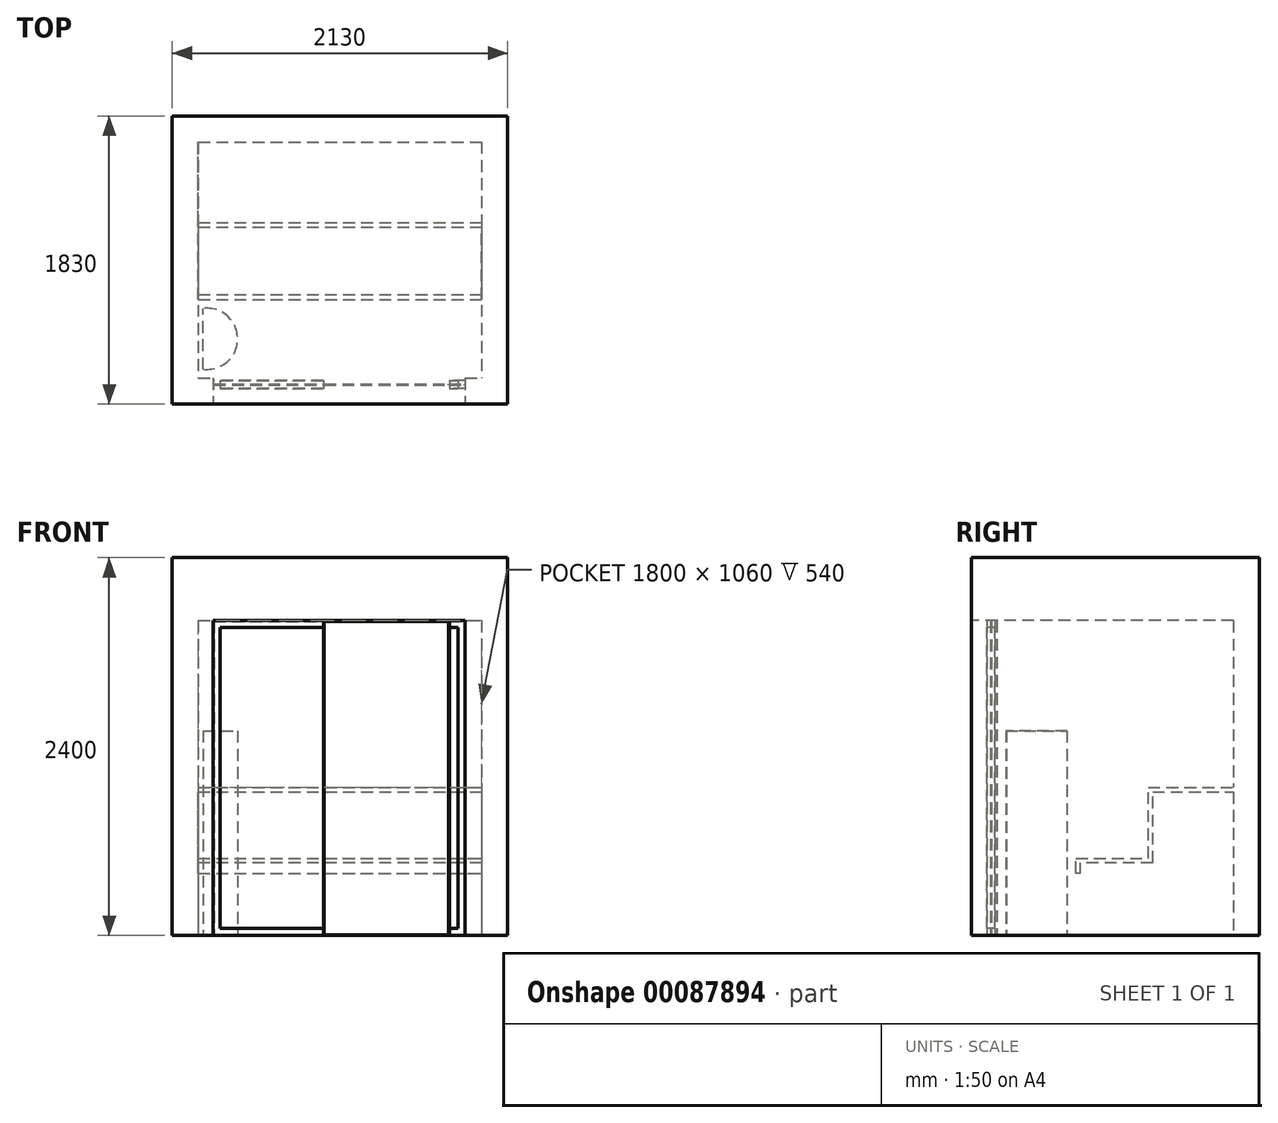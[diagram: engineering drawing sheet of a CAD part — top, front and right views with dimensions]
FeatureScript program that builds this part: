
annotation { "Feature Type Name" : "Feature", "Feature Type Description" : "" }
export const myFeature = defineFeature(function(context is Context, id is Id, definition is map)
    precondition{}
    {
        {
            var Q0;
            Q0=qCreatedBy(makeId("Top.planeOp"),FACE);
            var sketch = newSketch(context, id + "F0", { "sketchPlane" : qUnion([Q0])});
            skLineSegment(sketch, "E0.bottom", {"start": v(0, 0) * mm, "end": v(1800, 0) * mm});
            skLineSegment(sketch, "E0.top", {"start": v(0, -1500) * mm, "end": v(1800, -1500) * mm});
            skLineSegment(sketch, "E0.left", {"start": v(0, 0) * mm, "end": v(0, -1500) * mm});
            skLineSegment(sketch, "E0.right", {"start": v(1800, 0) * mm, "end": v(1800, -1500) * mm});
            skLineSegment(sketch, "E1.0", {"start": v(-165, -1665) * mm, "end": v(1965, -1665) * mm});
            skLineSegment(sketch, "E1.1", {"start": v(-165, 165) * mm, "end": v(-165, -1665) * mm});
            skLineSegment(sketch, "E1.2", {"start": v(-165, 165) * mm, "end": v(1965, 165) * mm});
            skLineSegment(sketch, "E1.3", {"start": v(1965, 165) * mm, "end": v(1965, -1665) * mm});
            skSolve(sketch);
        }
        {
            var Q0;
            Q0=makeQuery(id+"F0.imprint","IMPRINT",FACE,{"disambiguationData":[TD([[makeQuery(id+"F0.imprint","IMPRINT",EDGE,{"derivedFrom":sQuery(id+"F0.wireOp",EDGE,"E0.bottom")}),1.0]])]});
            extrude(context, id + "F1", {"entities" : qUnion([Q0]), "depth" : 2400 * mm});
        }
        {
            var Q0;
            Q0=makeQuery(id+"F1.opExtrude","SWEPT_FACE",FACE,{"disambiguationData":[OSD([sQuery(id+"F0.wireOp",EDGE,"E1.0")])]});
            var sketch = newSketch(context, id + "F2", { "sketchPlane" : qUnion([Q0])});
            skLineSegment(sketch, "E2", {"start": v(1695, 0) * mm, "end": v(1695, 2000) * mm});
            skLineSegment(sketch, "E3", {"start": v(1695, 2000) * mm, "end": v(95, 2000) * mm});
            skLineSegment(sketch, "E4", {"start": v(95, 2000) * mm, "end": v(95, 0) * mm});
            skLineSegment(sketch, "E5", {"start": v(95, 0) * mm, "end": v(1695, 0) * mm});
            skSolve(sketch);
        }
        {
            var Q0;
            Q0=makeQuery(id+"F2.imprint","IMPRINT",FACE,{"disambiguationData":[TD([[makeQuery(id+"F2.imprint","IMPRINT",EDGE,{"derivedFrom":sQuery(id+"F2.wireOp",EDGE,"E2")}),1.0]])]});
            extrude(context, id + "F3", {"entities" : qUnion([Q0]), "operationType" : NewBodyOperationType.REMOVE, "endBound" : BoundingType.UP_TO_NEXT, "oppositeDirection" : true, "depth" : 25 * mm});
        }
        {
            var Q0;
            Q0=makeQuery(id+"F1.opExtrude","CAP_FACE",FACE,{"disambiguationData":[OSD([sQuery(id+"F0.wireOp",EDGE,"E0.bottom"),sQuery(id+"F0.wireOp",EDGE,"E0.top"),sQuery(id+"F0.wireOp",EDGE,"E0.left"),sQuery(id+"F0.wireOp",EDGE,"E0.right"),sQuery(id+"F0.wireOp",EDGE,"E1.0"),sQuery(id+"F0.wireOp",EDGE,"E1.1"),sQuery(id+"F0.wireOp",EDGE,"E1.2"),sQuery(id+"F0.wireOp",EDGE,"E1.3")])],"isStart":false});
            var sketch = newSketch(context, id + "F4", { "sketchPlane" : qUnion([Q0])});
            skLineSegment(sketch, "E6.bottom", {"start": v(-165, 165) * mm, "end": v(1965, 165) * mm});
            skLineSegment(sketch, "E6.top", {"start": v(-165, -1665) * mm, "end": v(1965, -1665) * mm});
            skLineSegment(sketch, "E6.left", {"start": v(-165, 165) * mm, "end": v(-165, -1665) * mm});
            skLineSegment(sketch, "E6.right", {"start": v(1965, 165) * mm, "end": v(1965, -1665) * mm});
            skSolve(sketch);
        }
        {
            var Q0;
            Q0 = qSketchRegion(id + "F4", true);
            var Q1;
            Q1=makeQuery(id+"F3.boolean.opBoolean","COPY",FACE,{"derivedFrom":makeQuery(id+"F3.opExtrude","SWEPT_FACE",FACE,{"disambiguationData":[OSD([sQuery(id+"F2.wireOp",EDGE,"E3")])]})});
            extrude(context, id + "F5", {"entities" : qUnion([Q0]), "operationType" : NewBodyOperationType.ADD, "endBound" : BoundingType.UP_TO_SURFACE, "oppositeDirection" : true, "endBoundEntityFace" : qUnion([Q1]), "depth" : 25 * mm});
        }
        {
            var Q0;
            Q0=makeQuery(id+"F1.opExtrude","SWEPT_FACE",FACE,{"disambiguationData":[OSD([sQuery(id+"F0.wireOp",EDGE,"E1.0")])]});
            cPlane(context, id + "F6", {"entities" : qUnion([Q0]), "cplaneType" : CPlaneType.OFFSET, "offset" : 100 * mm, "oppositeDirection" : true, "width" : 150 * mm, "height" : 150 * mm});
        }
        {
            var Q0;
            Q0=qCreatedBy(id+"F6.planeOp",FACE);
            var sketch = newSketch(context, id + "F7", { "sketchPlane" : qUnion([Q0])});
            skLineSegment(sketch, "E7", {"start": v(140, 45) * mm, "end": v(140, 1955) * mm});
            skLineSegment(sketch, "E8", {"start": v(140, 1955) * mm, "end": v(795, 1955) * mm});
            skLineSegment(sketch, "E9", {"start": v(1650, 1955) * mm, "end": v(1650, 45) * mm});
            skLineSegment(sketch, "E10", {"start": v(1695, 0) * mm, "end": v(1695, 2000) * mm});
            skLineSegment(sketch, "E11", {"start": v(1695, 2000) * mm, "end": v(1595, 2000) * mm});
            skLineSegment(sketch, "E12", {"start": v(95, 2000) * mm, "end": v(95, 0) * mm});
            skLineSegment(sketch, "E13", {"start": v(795, 2000) * mm, "end": v(795, 1955) * mm});
            skLineSegment(sketch, "E14", {"start": v(1595, 2000) * mm, "end": v(1595, 1955) * mm});
            skLineSegment(sketch, "E15.trimOffspring", {"start": v(795, 2000) * mm, "end": v(95, 2000) * mm});
            skLineSegment(sketch, "E16.trimOffspring", {"start": v(1595, 1955) * mm, "end": v(1650, 1955) * mm});
            skLineSegment(sketch, "E17", {"start": v(140, 45) * mm, "end": v(795, 45) * mm});
            skLineSegment(sketch, "E18", {"start": v(795, 45) * mm, "end": v(795, 0) * mm});
            skLineSegment(sketch, "E19", {"start": v(95, 0) * mm, "end": v(795, 0) * mm});
            skLineSegment(sketch, "E20", {"start": v(1695, 0) * mm, "end": v(1595, 0) * mm});
            skLineSegment(sketch, "E21", {"start": v(1595, 0) * mm, "end": v(1595, 45) * mm});
            skLineSegment(sketch, "E22", {"start": v(1595, 45) * mm, "end": v(1650, 45) * mm});
            skPoint(sketch, "E23.orphan", {"position": v(1650, 0) * mm});
            skSolve(sketch);
        }
        {
            var Q0;
            Q0 = qSketchRegion(id + "F7", true);
            extrude(context, id + "F8", {"entities" : qUnion([Q0]), "oppositeDirection" : true, "depth" : 50 * mm});
        }
        {
            var Q0;
            Q0=makeQuery(id+"F8.opExtrude","CAP_FACE",FACE,{"disambiguationData":[OSD([sQuery(id+"F7.wireOp",EDGE,"E7"),sQuery(id+"F7.wireOp",EDGE,"E8"),sQuery(id+"F7.wireOp",EDGE,"E12"),sQuery(id+"F7.wireOp",EDGE,"E13"),sQuery(id+"F7.wireOp",EDGE,"E15.trimOffspring"),sQuery(id+"F7.wireOp",EDGE,"E17"),sQuery(id+"F7.wireOp",EDGE,"E18"),sQuery(id+"F7.wireOp",EDGE,"E19")])],"isStart":true});
            cPlane(context, id + "F9", {"entities" : qUnion([Q0]), "cplaneType" : CPlaneType.OFFSET, "offset" : 25 * mm, "oppositeDirection" : true, "width" : 150 * mm, "height" : 150 * mm});
        }
        {
            var Q0;
            Q0=qCreatedBy(id+"F9.planeOp",FACE);
            var sketch = newSketch(context, id + "F10", { "sketchPlane" : qUnion([Q0])});
            skLineSegment(sketch, "E24.bottom", {"start": v(100, 1995) * mm, "end": v(795, 1995) * mm});
            skLineSegment(sketch, "E24.top", {"start": v(100, 5) * mm, "end": v(795, 5) * mm});
            skLineSegment(sketch, "E24.left", {"start": v(100, 1995) * mm, "end": v(100, 5) * mm});
            skLineSegment(sketch, "E24.right", {"start": v(795, 1995) * mm, "end": v(795, 5) * mm});
            skLineSegment(sketch, "E25.bottom", {"start": v(800, 1995) * mm, "end": v(1590, 1995) * mm});
            skLineSegment(sketch, "E25.top", {"start": v(800, 5) * mm, "end": v(1590, 5) * mm});
            skLineSegment(sketch, "E25.left", {"start": v(800, 1995) * mm, "end": v(800, 5) * mm});
            skLineSegment(sketch, "E25.right", {"start": v(1590, 1995) * mm, "end": v(1590, 5) * mm});
            skLineSegment(sketch, "E26.bottom", {"start": v(1595, 5) * mm, "end": v(1690, 5) * mm});
            skLineSegment(sketch, "E26.top", {"start": v(1595, 1995) * mm, "end": v(1690, 1995) * mm});
            skLineSegment(sketch, "E26.left", {"start": v(1595, 5) * mm, "end": v(1595, 1995) * mm});
            skLineSegment(sketch, "E26.right", {"start": v(1690, 5) * mm, "end": v(1690, 1995) * mm});
            skSolve(sketch);
        }
        {
            var Q0;
            Q0 = qSketchRegion(id + "F10", true);
            extrude(context, id + "F11", {"entities" : qUnion([Q0]), "endBound" : BoundingType.SYMMETRIC, "depth" : 6 * mm});
        }
        {
            var Q0;
            Q0=makeQuery(id+"F1.opExtrude","SWEPT_FACE",FACE,{"disambiguationData":[OSD([sQuery(id+"F0.wireOp",EDGE,"E0.right")])]});
            var sketch = newSketch(context, id + "F12", { "sketchPlane" : qUnion([Q0])});
            skLineSegment(sketch, "E27.bottom", {"start": v(0, 940) * mm, "end": v(540, 940) * mm});
            skLineSegment(sketch, "E27.top", {"start": v(0, 912) * mm, "end": v(540, 912) * mm});
            skLineSegment(sketch, "E27.left", {"start": v(0, 940) * mm, "end": v(0, 912) * mm});
            skLineSegment(sketch, "E27.right", {"start": v(540, 940) * mm, "end": v(540, 912) * mm});
            skSolve(sketch);
        }
        {
            var Q0;
            Q0 = qSketchRegion(id + "F12", true);
            extrude(context, id + "F13", {"entities" : qUnion([Q0]), "endBound" : BoundingType.UP_TO_NEXT, "depth" : 25 * mm});
        }
        {
            var Q0;
            Q0=makeQuery(id+"F13.opExtrude","SWEPT_FACE",FACE,{"disambiguationData":[OSD([sQuery(id+"F12.wireOp",EDGE,"E27.right")])]});
            var sketch = newSketch(context, id + "F14", { "sketchPlane" : qUnion([Q0])});
            skLineSegment(sketch, "E28.bottom", {"start": v(0, 940) * mm, "end": v(1800, 940) * mm});
            skLineSegment(sketch, "E28.top", {"start": v(0, 462) * mm, "end": v(1800, 462) * mm});
            skLineSegment(sketch, "E28.left", {"start": v(0, 940) * mm, "end": v(0, 462) * mm});
            skLineSegment(sketch, "E28.right", {"start": v(1800, 940) * mm, "end": v(1800, 462) * mm});
            skSolve(sketch);
        }
        {
            var Q0;
            Q0 = qSketchRegion(id + "F14", true);
            extrude(context, id + "F15", {"entities" : qUnion([Q0]), "operationType" : NewBodyOperationType.ADD, "oppositeDirection" : true, "depth" : 28 * mm});
        }
        {
            var Q0;
            Q0=makeQuery(id+"F15.boolean.opBoolean","MERGE",FACE,{"derivedFrom":[makeQuery(id+"F13.opExtrude","SWEPT_FACE",FACE,{"disambiguationData":[OSD([sQuery(id+"F12.wireOp",EDGE,"E27.right")])]}),makeQuery(id+"F15.opExtrude","CAP_FACE",FACE,{"disambiguationData":[OSD([sQuery(id+"F14.wireOp",EDGE,"E28.bottom"),sQuery(id+"F14.wireOp",EDGE,"E28.top"),sQuery(id+"F14.wireOp",EDGE,"E28.left"),sQuery(id+"F14.wireOp",EDGE,"E28.right")])],"isStart":true})]});
            var sketch = newSketch(context, id + "F16", { "sketchPlane" : qUnion([Q0])});
            skLineSegment(sketch, "E29.bottom", {"start": v(0, 462) * mm, "end": v(1800, 462) * mm});
            skLineSegment(sketch, "E29.top", {"start": v(0, 490) * mm, "end": v(1800, 490) * mm});
            skLineSegment(sketch, "E29.left", {"start": v(0, 462) * mm, "end": v(0, 490) * mm});
            skLineSegment(sketch, "E29.right", {"start": v(1800, 462) * mm, "end": v(1800, 490) * mm});
            skSolve(sketch);
        }
        {
            var Q0;
            Q0 = qSketchRegion(id + "F16", true);
            extrude(context, id + "F17", {"entities" : qUnion([Q0]), "operationType" : NewBodyOperationType.ADD, "depth" : 460 * mm});
        }
        {
            var Q0;
            Q0=makeQuery(id+"F17.opExtrude","CAP_FACE",FACE,{"disambiguationData":[OSD([sQuery(id+"F16.wireOp",EDGE,"E29.bottom"),sQuery(id+"F16.wireOp",EDGE,"E29.top"),sQuery(id+"F16.wireOp",EDGE,"E29.left"),sQuery(id+"F16.wireOp",EDGE,"E29.right")])],"isStart":false});
            var sketch = newSketch(context, id + "F18", { "sketchPlane" : qUnion([Q0])});
            skLineSegment(sketch, "E30.bottom", {"start": v(0, 490) * mm, "end": v(1800, 490) * mm});
            skLineSegment(sketch, "E30.top", {"start": v(0, 395) * mm, "end": v(1800, 395) * mm});
            skLineSegment(sketch, "E30.left", {"start": v(0, 490) * mm, "end": v(0, 395) * mm});
            skLineSegment(sketch, "E30.right", {"start": v(1800, 490) * mm, "end": v(1800, 395) * mm});
            skSolve(sketch);
        }
        {
            var Q0;
            Q0 = qSketchRegion(id + "F18", true);
            extrude(context, id + "F19", {"entities" : qUnion([Q0]), "operationType" : NewBodyOperationType.ADD, "oppositeDirection" : true, "depth" : 28 * mm});
        }
        {
            var Q0;
            Q0=makeQuery(id+"F1.opExtrude","CAP_FACE",FACE,{"disambiguationData":[OSD([sQuery(id+"F0.wireOp",EDGE,"E0.bottom"),sQuery(id+"F0.wireOp",EDGE,"E0.top"),sQuery(id+"F0.wireOp",EDGE,"E0.left"),sQuery(id+"F0.wireOp",EDGE,"E0.right"),sQuery(id+"F0.wireOp",EDGE,"E1.0"),sQuery(id+"F0.wireOp",EDGE,"E1.1"),sQuery(id+"F0.wireOp",EDGE,"E1.2"),sQuery(id+"F0.wireOp",EDGE,"E1.3")])],"isStart":true});
            var sketch = newSketch(context, id + "F20", { "sketchPlane" : qUnion([Q0])});
            skArc(sketch, "E31", {"start": v(30, 1057.5) * mm, "mid": v(250, 1250) * mm, "end": v(30, 1442.5) * mm});
            skLineSegment(sketch, "E32", {"start": v(30, 1442.5) * mm, "end": v(30, 1057.5) * mm});
            skLineSegment(sketch, "E33", {"start": v(250, 1428.99) * mm, "end": v(250, 1137.54) * mm, "construction": true});
            skSolve(sketch);
        }
        {
            var Q0;
            Q0=makeQuery(id+"F20.imprint","IMPRINT",FACE,{"disambiguationData":[TD([[makeQuery(id+"F20.imprint","IMPRINT",EDGE,{"derivedFrom":sQuery(id+"F20.wireOp",EDGE,"E31")}),1.0]])]});
            extrude(context, id + "F21", {"entities" : qUnion([Q0]), "oppositeDirection" : true, "depth" : 1300 * mm});
        }
    });
